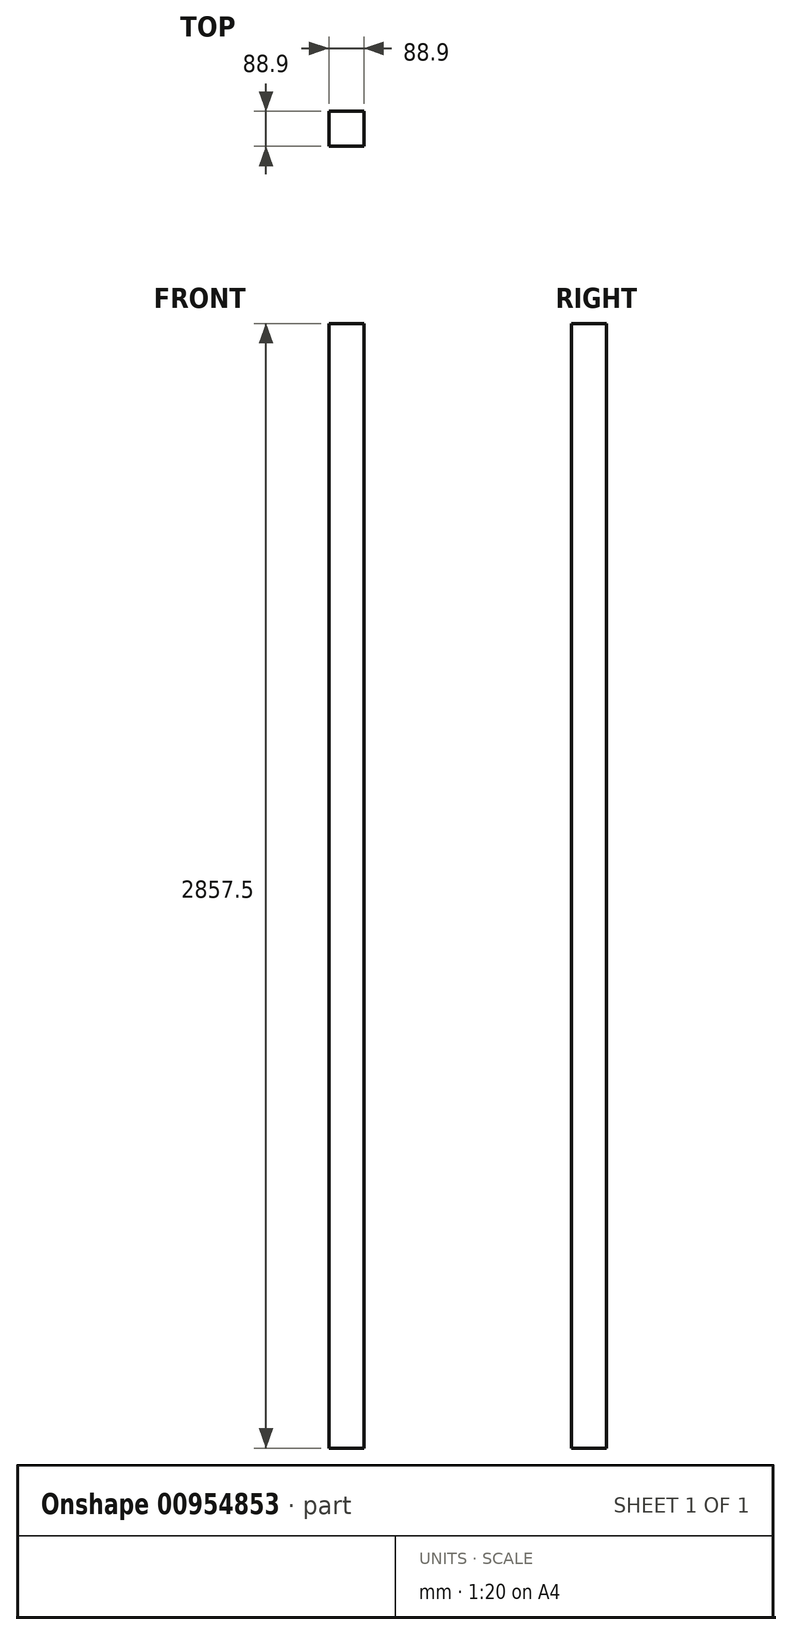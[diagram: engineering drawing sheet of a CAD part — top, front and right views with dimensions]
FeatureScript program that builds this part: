
annotation { "Feature Type Name" : "Feature", "Feature Type Description" : "" }
export const myFeature = defineFeature(function(context is Context, id is Id, definition is map)
    precondition{}
    {
        {
            var Q0;
            Q0=qCreatedBy(makeId("Top.planeOp"),FACE);
            var sketch = newSketch(context, id + "F0", { "sketchPlane" : qUnion([Q0])});
            skLineSegment(sketch, "E0.bottom", {"start": v(-44.45, 44.45) * mm, "end": v(44.45, 44.45) * mm});
            skLineSegment(sketch, "E0.top", {"start": v(-44.45, -44.45) * mm, "end": v(44.45, -44.45) * mm});
            skLineSegment(sketch, "E0.left", {"start": v(-44.45, 44.45) * mm, "end": v(-44.45, -44.45) * mm});
            skLineSegment(sketch, "E0.right", {"start": v(44.45, 44.45) * mm, "end": v(44.45, -44.45) * mm});
            skPoint(sketch, "E1", {"position": v(-44.45, 0) * mm});
            skPoint(sketch, "E2", {"position": v(0, 44.45) * mm});
            skSolve(sketch);
        }
        {
            var Q0;
            Q0=qSketchRegion(id+"F0",true);
            extrude(context, id + "F1", {"entities" : qUnion([Q0]), "depth" : 2247.9 * mm, "offsetDistance" : 25.4 * mm, "hasSecondDirection" : true, "secondDirectionOppositeDirection" : true, "secondDirectionDepth" : 609.6 * mm});
        }
    });
